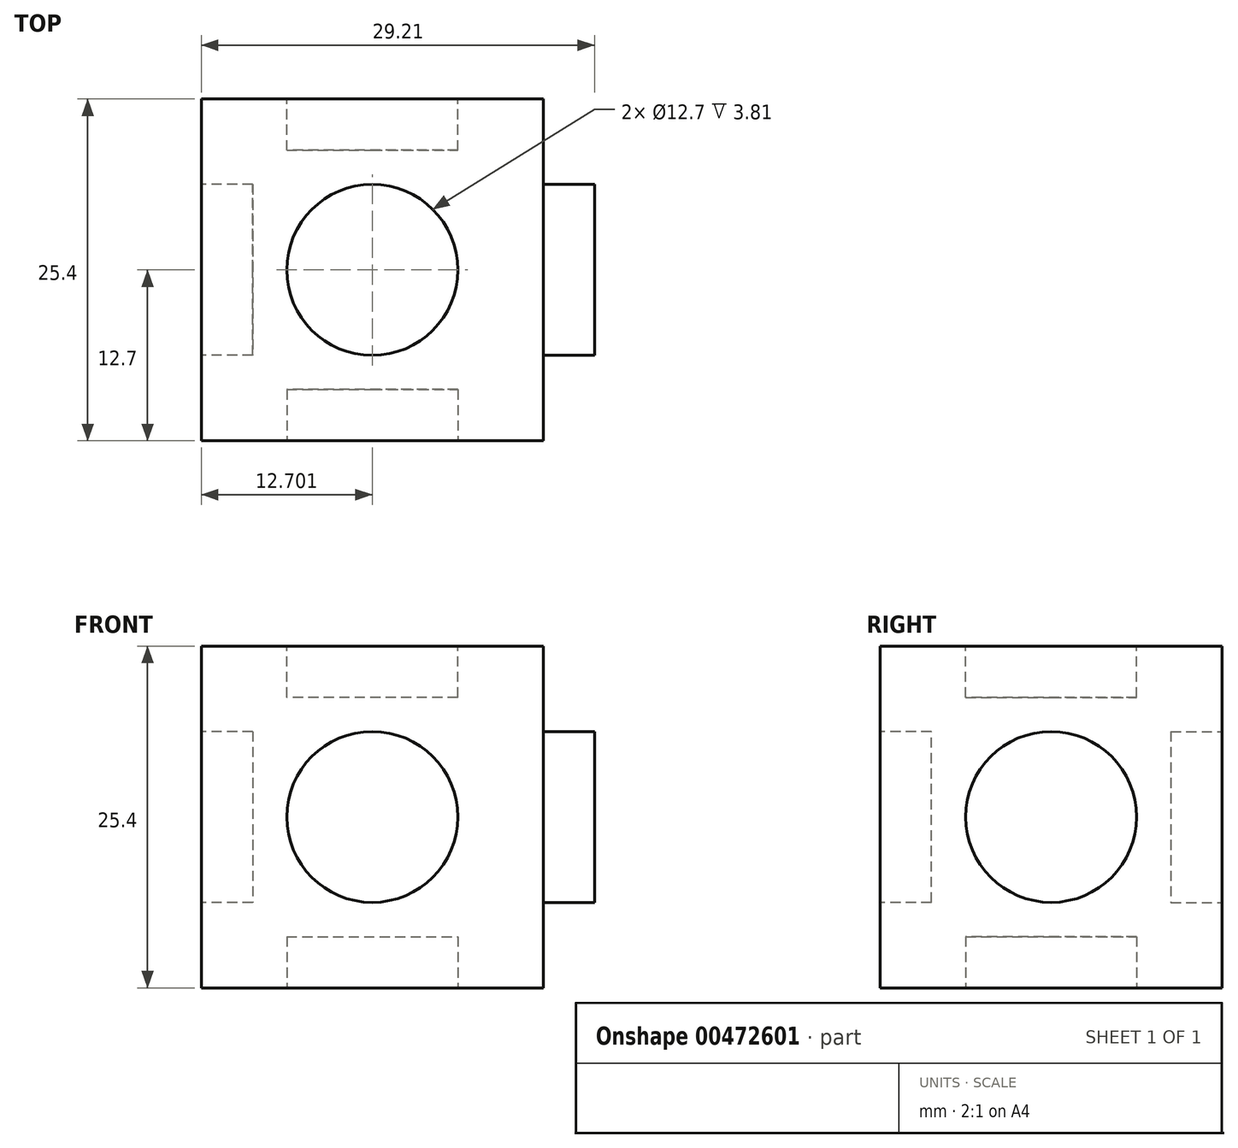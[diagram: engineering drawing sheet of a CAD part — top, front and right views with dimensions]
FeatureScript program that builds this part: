
annotation { "Feature Type Name" : "Feature", "Feature Type Description" : "" }
export const myFeature = defineFeature(function(context is Context, id is Id, definition is map)
    precondition{}
    {
        {
            var Q0;
            Q0=qCreatedBy(makeId("Front.planeOp"),FACE);
            var sketch = newSketch(context, id + "F0", { "sketchPlane" : qUnion([Q0])});
            skLineSegment(sketch, "E0.bottom", {"start": v(-6.95, 0.68) * mm, "end": v(18.45, 0.68) * mm});
            skLineSegment(sketch, "E0.top", {"start": v(-6.95, -24.72) * mm, "end": v(18.45, -24.72) * mm});
            skLineSegment(sketch, "E0.left", {"start": v(-6.95, 0.68) * mm, "end": v(-6.95, -24.72) * mm});
            skLineSegment(sketch, "E0.right", {"start": v(18.45, 0.68) * mm, "end": v(18.45, -24.72) * mm});
            skSolve(sketch);
        }
        {
            var Q0;
            Q0 = qSketchRegion(id + "F0", true);
            extrude(context, id + "F1", {"entities" : qUnion([Q0]), "depth" : 25.4 * mm});
        }
        {
            var Q0;
            Q0=makeQuery(id+"F1.opExtrude","CAP_FACE",FACE,{"disambiguationData":[OSD([sQuery(id+"F0.wireOp",EDGE,"E0.bottom"),sQuery(id+"F0.wireOp",EDGE,"E0.top"),sQuery(id+"F0.wireOp",EDGE,"E0.left"),sQuery(id+"F0.wireOp",EDGE,"E0.right")])],"isStart":false});
            var sketch = newSketch(context, id + "F2", { "sketchPlane" : qUnion([Q0])});
            skCircle(sketch, "E1", {"center": v(5.75, -12.02) * mm, "radius": 6.35 * mm});
            skSolve(sketch);
        }
        {
            var Q0;
            Q0=makeQuery(id+"F1.opExtrude","SWEPT_FACE",FACE,{"disambiguationData":[OSD([sQuery(id+"F0.wireOp",EDGE,"E0.top")])]});
            var sketch = newSketch(context, id + "F3", { "sketchPlane" : qUnion([Q0])});
            skCircle(sketch, "E2", {"center": v(5.75, 12.7) * mm, "radius": 6.35 * mm});
            skSolve(sketch);
        }
        {
            var Q0;
            Q0=makeQuery(id+"F1.opExtrude","SWEPT_FACE",FACE,{"disambiguationData":[OSD([sQuery(id+"F0.wireOp",EDGE,"E0.right")])]});
            var sketch = newSketch(context, id + "F4", { "sketchPlane" : qUnion([Q0])});
            skCircle(sketch, "E3", {"center": v(-12.7, -12.02) * mm, "radius": 6.35 * mm});
            skSolve(sketch);
        }
        {
            var Q0;
            Q0=makeQuery(id+"F1.opExtrude","SWEPT_FACE",FACE,{"disambiguationData":[OSD([sQuery(id+"F0.wireOp",EDGE,"E0.bottom")])]});
            var sketch = newSketch(context, id + "F5", { "sketchPlane" : qUnion([Q0])});
            skCircle(sketch, "E4", {"center": v(5.75, -12.7) * mm, "radius": 6.35 * mm});
            skSolve(sketch);
        }
        {
            var Q0;
            Q0=makeQuery(id+"F1.opExtrude","SWEPT_FACE",FACE,{"disambiguationData":[OSD([sQuery(id+"F0.wireOp",EDGE,"E0.left")])]});
            var sketch = newSketch(context, id + "F6", { "sketchPlane" : qUnion([Q0])});
            skCircle(sketch, "E5", {"center": v(12.7, -12.02) * mm, "radius": 6.35 * mm});
            skSolve(sketch);
        }
        {
            var Q0;
            Q0=makeQuery(id+"F1.opExtrude","CAP_FACE",FACE,{"disambiguationData":[OSD([sQuery(id+"F0.wireOp",EDGE,"E0.bottom"),sQuery(id+"F0.wireOp",EDGE,"E0.top"),sQuery(id+"F0.wireOp",EDGE,"E0.left"),sQuery(id+"F0.wireOp",EDGE,"E0.right")])],"isStart":true});
            var sketch = newSketch(context, id + "F7", { "sketchPlane" : qUnion([Q0])});
            skCircle(sketch, "E6", {"center": v(-5.75, -12.02) * mm, "radius": 6.35 * mm});
            skSolve(sketch);
        }
        {
            var Q0;
            Q0 = qSketchRegion(id + "F7", true);
            extrude(context, id + "F8", {"entities" : qUnion([Q0]), "operationType" : NewBodyOperationType.REMOVE, "oppositeDirection" : true, "depth" : 3.8 * mm});
        }
        {
            var Q0;
            Q0 = qSketchRegion(id + "F6", true);
            extrude(context, id + "F9", {"entities" : qUnion([Q0]), "operationType" : NewBodyOperationType.REMOVE, "oppositeDirection" : true, "depth" : 3.8 * mm});
        }
        {
            var Q0;
            Q0 = qSketchRegion(id + "F5", true);
            extrude(context, id + "F10", {"entities" : qUnion([Q0]), "operationType" : NewBodyOperationType.REMOVE, "oppositeDirection" : true, "depth" : 3.8 * mm});
        }
        {
            var Q0;
            Q0 = qSketchRegion(id + "F4", true);
            extrude(context, id + "F11", {"entities" : qUnion([Q0]), "operationType" : NewBodyOperationType.ADD, "depth" : 3.8 * mm});
        }
        {
            var Q0;
            Q0 = qSketchRegion(id + "F3", true);
            extrude(context, id + "F12", {"entities" : qUnion([Q0]), "operationType" : NewBodyOperationType.REMOVE, "oppositeDirection" : true, "depth" : 3.8 * mm});
        }
        {
            var Q0;
            Q0 = qSketchRegion(id + "F2", true);
            extrude(context, id + "F13", {"entities" : qUnion([Q0]), "operationType" : NewBodyOperationType.REMOVE, "oppositeDirection" : true, "depth" : 3.8 * mm});
        }
    });
